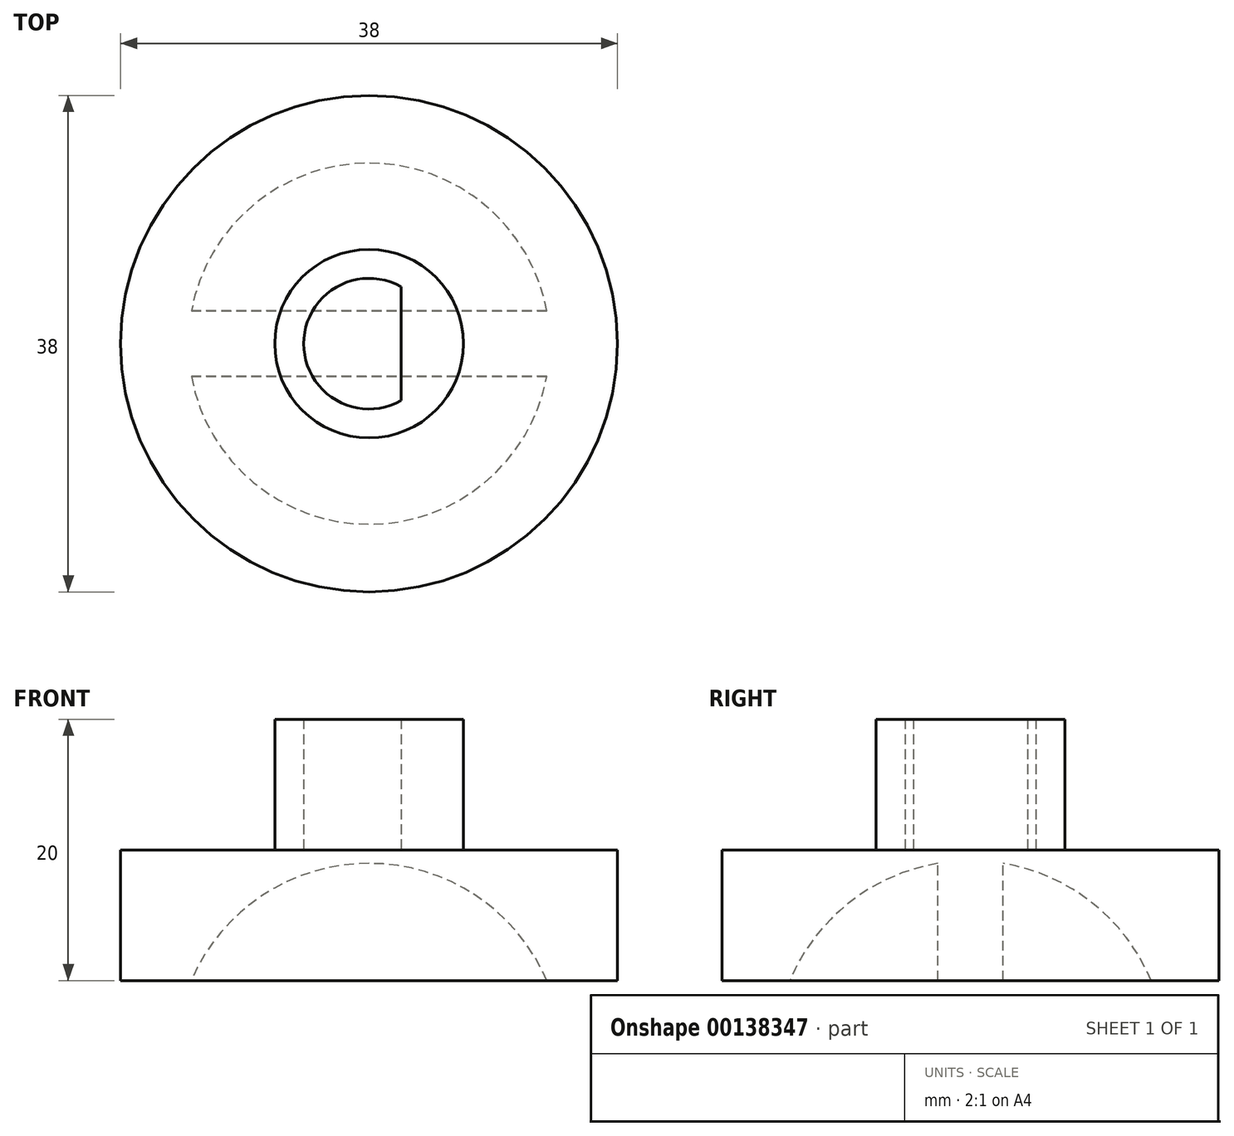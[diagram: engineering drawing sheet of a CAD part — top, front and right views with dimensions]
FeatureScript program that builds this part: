
annotation { "Feature Type Name" : "Feature", "Feature Type Description" : "" }
export const myFeature = defineFeature(function(context is Context, id is Id, definition is map)
    precondition{}
    {
        {
            var Q0;
            Q0=qCreatedBy(makeId("Top.planeOp"),FACE);
            var sketch = newSketch(context, id + "F0", { "sketchPlane" : qUnion([Q0])});
            skCircle(sketch, "E0", {"center": v(0, 0) * mm, "radius": 5 * mm});
            skCircle(sketch, "E1", {"center": v(0, 0) * mm, "radius": 7.21 * mm});
            skLineSegment(sketch, "E2", {"start": v(2.45, 4.36) * mm, "end": v(2.45, -4.36) * mm});
            skSolve(sketch);
        }
        {
            var Q0;
            Q0 = qSketchRegion(id + "F0", true);
            extrude(context, id + "F1", {"entities" : qUnion([Q0]), "depth" : 10 * mm});
        }
        {
            var Q0;
            {var subQ0=sQuery(id+"F0.wireOp",EDGE,"E2");Q0=makeQuery(id+"F0.imprint","IMPRINT",FACE,{"disambiguationData":[TD([[makeQuery(id+"F0.imprint","IMPRINT",EDGE,{"derivedFrom":subQ0}),1.0]])]});}
            extrude(context, id + "F2", {"entities" : qUnion([Q0]), "operationType" : NewBodyOperationType.ADD, "depth" : 10 * mm});
        }
        {
            var Q0;
            Q0=qCreatedBy(makeId("Top.planeOp"),FACE);
            var sketch = newSketch(context, id + "F3", { "sketchPlane" : qUnion([Q0])});
            skCircle(sketch, "E3", {"center": v(0, 0) * mm, "radius": 19 * mm});
            skSolve(sketch);
        }
        {
            var Q0;
            Q0 = qSketchRegion(id + "F3", true);
            extrude(context, id + "F4", {"entities" : qUnion([Q0]), "operationType" : NewBodyOperationType.ADD, "oppositeDirection" : true, "offsetDistance" : 25 * mm, "depth" : 10 * mm});
        }
        {
            var Q0;
            Q0=qCreatedBy(makeId("Front.planeOp"),FACE);
            var sketch = newSketch(context, id + "F5", { "sketchPlane" : qUnion([Q0])});
            skPoint(sketch, "E4", {"position": v(0, -0.82) * mm});
            skPoint(sketch, "E5", {"position": v(0, -15.82) * mm});
            skCircle(sketch, "E6", {"center": v(0, -15.82) * mm, "radius": 15 * mm});
            skLineSegment(sketch, "E7", {"start": v(0, -0.82) * mm, "end": v(0, -30.82) * mm});
            skSolve(sketch);
        }
        {
            var Q0;
            {var subQ0=sQuery(id+"F5.wireOp",EDGE,"E7");Q0=makeQuery(id+"F5.imprint","IMPRINT",FACE,{"disambiguationData":[TD([[makeQuery(id+"F5.imprint","IMPRINT",EDGE,{"derivedFrom":subQ0}),-1.0]])]});}
            var Q1;
            Q1=sQuery(id+"F5.wireOp",EDGE,"E7");
            revolve(context, id + "F6", {"operationType" : NewBodyOperationType.REMOVE, "surfaceOperationType" : NewSurfaceOperationType.NEW, "entities" : qUnion([Q0]), "axis" : qUnion([Q1]), "revolveType" : RevolveType.FULL});
        }
        {
            var Q0;
            Q0 = qSketchRegion(id + "F5", true);
            extrude(context, id + "F7", {"entities" : qUnion([Q0]), "operationType" : NewBodyOperationType.ADD, "depth" : 2.5 * mm, "offsetDistance" : 25 * mm});
        }
        {
            var Q0;
            Q0=makeQuery(id+"F7.opExtrude","CAP_FACE",FACE,{"disambiguationData":[OSD([sQuery(id+"F5.wireOp",EDGE,"E6")])],"isStart":true});
            extrude(context, id + "F8", {"entities" : qUnion([Q0]), "operationType" : NewBodyOperationType.ADD, "depth" : 2.5 * mm, "offsetDistance" : 25 * mm});
        }
        {
            var Q0;
            Q0=makeQuery(id+"F4.opExtrude","CAP_FACE",FACE,{"disambiguationData":[OSD([sQuery(id+"F3.wireOp",EDGE,"E3")])],"isStart":false});
            var sketch = newSketch(context, id + "F9", { "sketchPlane" : qUnion([Q0])});
            skCircle(sketch, "E8", {"center": v(0, 0) * mm, "radius": 20.25 * mm});
            skSolve(sketch);
        }
        {
            var Q0;
            Q0 = qSketchRegion(id + "F9", true);
            extrude(context, id + "F10", {"entities" : qUnion([Q0]), "operationType" : NewBodyOperationType.REMOVE, "endBound" : BoundingType.UP_TO_NEXT, "depth" : 20 * mm, "offsetDistance" : 25 * mm});
        }
    });
